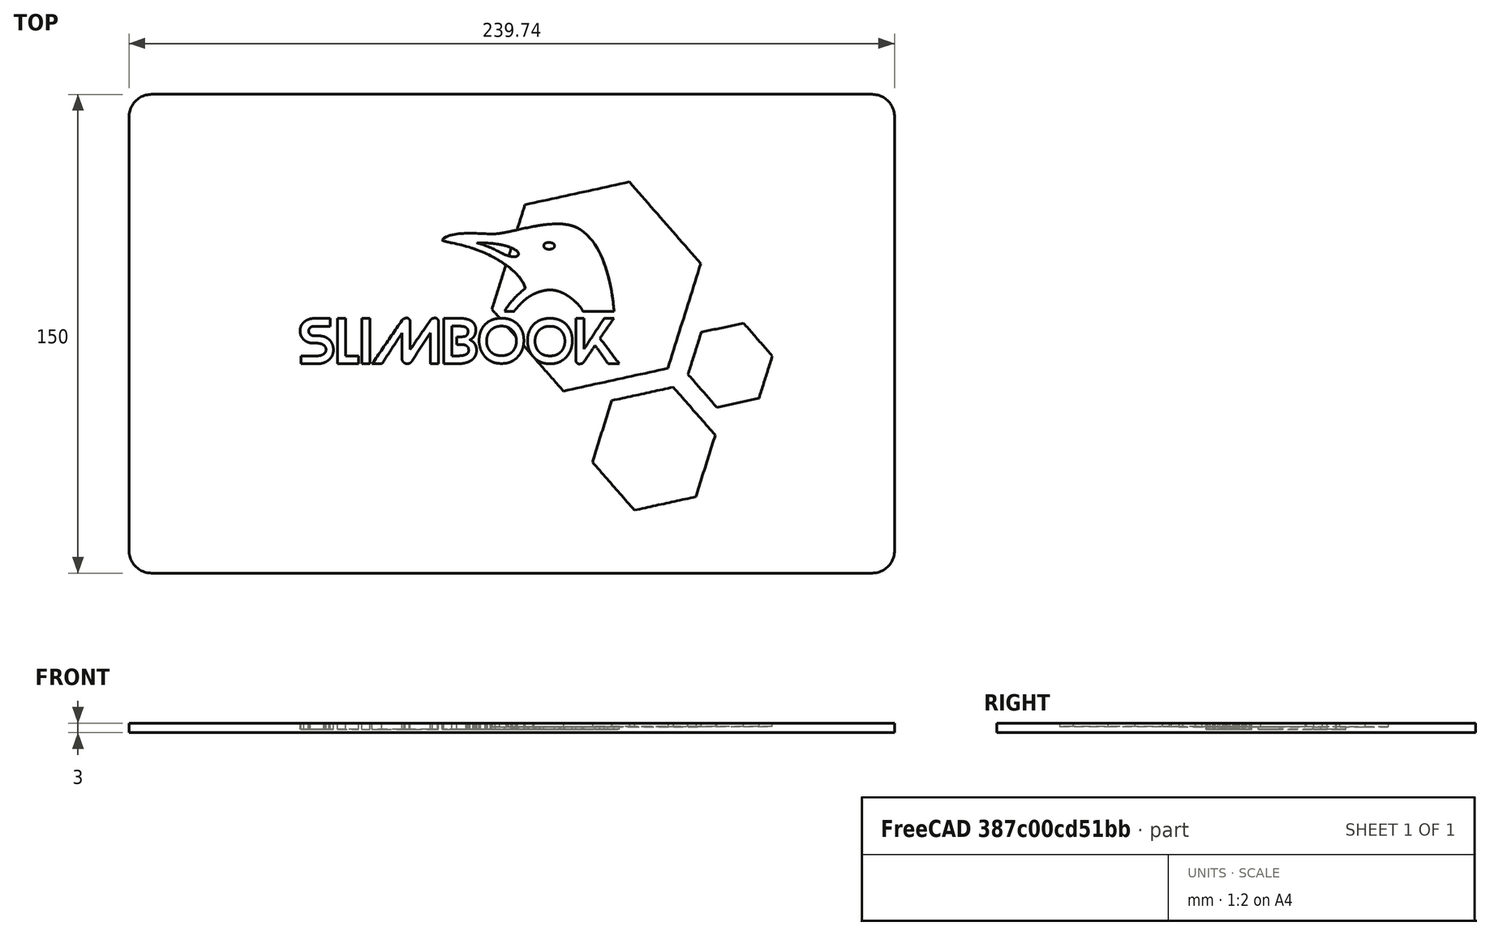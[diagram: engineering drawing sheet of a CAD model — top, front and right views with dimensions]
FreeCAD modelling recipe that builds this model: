
FCSTD DOCUMENT  (FreeCAD 0.20R29603 (Git))
Label: TAPA-CAJA-slimbook
License: All rights reserved
LicenseURL: http://en.wikipedia.org/wiki/All_rights_reserved
objects: Part::Feature×32, Part::Face×29, Part::Cut×12, Part::Extrusion×5, Part::MultiFuse×2, Part::FeaturePython×1
note: 81 computed .brp shape members not serialized (recipe doc carries the construction recipe); baked Part::Feature solids carry a one-line shape summary decoded from their .brp

FEATURE [Part::Feature] rect4531
  shape: bbox 239.7 x 150 x 2e-07 mm, 0 faces, 0 solids (baked)
FEATURE [Part::Feature] path1385_9
  shape: bbox 38.48 x 38.56 x 2.028e-07 mm, 0 faces, 0 solids (baked)
FEATURE [Part::Feature] path1385_9_8
  shape: bbox 26.41 x 26.4 x 2e-07 mm, 0 faces, 0 solids (baked)
FEATURE [Part::Feature] path4723003
  shape: bbox 54.7 x 27.53 x 2.667e-07 mm, 0 faces, 0 solids (baked)
FEATURE [Part::Face] Face001
  FaceMakerClass = Part::FaceMakerBullseye
  Sources = -> [path4723003]
FEATURE [Part::Feature] path4723004
  shape: bbox 3.528 x 2.127 x 2.667e-07 mm, 0 faces, 0 solids (baked)
FEATURE [Part::Feature] path4723005
  shape: bbox 13.37 x 4.768 x 2.667e-07 mm, 0 faces, 0 solids (baked)
FEATURE [Part::Face] Face002
  FaceMakerClass = Part::FaceMakerBullseye
  Sources = -> [path4723004,path4723005]
FEATURE [Part::Cut] Cut035
  Base = -> Face001
  Refine = true
  Tool = -> Face002
FEATURE [Part::Feature] path4723006
  shape: bbox 20.8 x 14.35 x 2.667e-07 mm, 0 faces, 0 solids (baked)
FEATURE [Part::Face] Face003
  FaceMakerClass = Part::FaceMakerBullseye
  Sources = -> [path4723006]
FEATURE [Part::Feature] path4723007
  shape: bbox 13.53 x 14.33 x 2.667e-07 mm, 0 faces, 0 solids (baked)
FEATURE [Part::Face] Face004
  FaceMakerClass = Part::FaceMakerBullseye
  Sources = -> [path4723007]
FEATURE [Part::Feature] path4723008
  shape: bbox 14.02 x 14.18 x 2.667e-07 mm, 0 faces, 0 solids (baked)
FEATURE [Part::Face] Face005
  FaceMakerClass = Part::FaceMakerBullseye
  Sources = -> [path4723008]
FEATURE [Part::Feature] path4723009
  shape: bbox 10.29 x 14.24 x 2.667e-07 mm, 0 faces, 0 solids (baked)
FEATURE [Part::Face] Face010
  FaceMakerClass = Part::FaceMakerBullseye
  Sources = -> [path4723009]
FEATURE [Part::Feature] path4723010
  shape: bbox 10.44 x 14.24 x 2.667e-07 mm, 0 faces, 0 solids (baked)
FEATURE [Part::Face] Face013
  FaceMakerClass = Part::FaceMakerBullseye
  Sources = -> [path4723010]
FEATURE [Part::Feature] path4723011
  shape: bbox 6.55 x 14.24 x 2.667e-07 mm, 0 faces, 0 solids (baked)
FEATURE [Part::Face] Face012
  FaceMakerClass = Part::FaceMakerBullseye
  Sources = -> [path4723011]
FEATURE [Part::Feature] path4723012
  shape: bbox 2.568 x 14.24 x 2.667e-07 mm, 0 faces, 0 solids (baked)
FEATURE [Part::Face] Face011
  FaceMakerClass = Part::FaceMakerBullseye
  Sources = -> [path4723012]
FEATURE [Part::Feature] path4723013
  shape: bbox 14.02 x 14.24 x 2.667e-07 mm, 0 faces, 0 solids (baked)
FEATURE [Part::Face] Face008
  FaceMakerClass = Part::FaceMakerBullseye
  Sources = -> [path4723013]
FEATURE [Part::Feature] path4723014
  shape: bbox 5.247 x 9.291 x 2.667e-07 mm, 0 faces, 0 solids (baked)
FEATURE [Part::Face] Face009
  FaceMakerClass = Part::FaceMakerBullseye
  Sources = -> [path4723014]
FEATURE [Part::Cut] Cut038
  Base = -> Face010
  Refine = true
  Tool = -> Face009
FEATURE [Part::Feature] path4723015
  shape: bbox 9.343 x 9.236 x 2.667e-07 mm, 0 faces, 0 solids (baked)
FEATURE [Part::Face] Face006
  FaceMakerClass = Part::FaceMakerBullseye
  Sources = -> [path4723015]
FEATURE [Part::Cut] Cut036
  Base = -> Face005
  Refine = true
  Tool = -> Face006
FEATURE [Part::Feature] path4723016
  shape: bbox 9.342 x 9.272 x 2.667e-07 mm, 0 faces, 0 solids (baked)
FEATURE [Part::Face] Face007
  FaceMakerClass = Part::FaceMakerBullseye
  Sources = -> [path4723016]
FEATURE [Part::Cut] Cut037
  Base = -> Face008
  Refine = true
  Tool = -> Face007
FEATURE [Part::MultiFuse] Fusion027  label="logo_pinguino"
  Placement = pos=(189,115,0) rot=(0.707107,-0.707107,0;3.14159rad)
  Refine = true
  Shapes = -> [Face013,Cut035,Face003,Face004,Cut036,Cut037,Cut038,Face011,Face012]
FEATURE [Part::Extrusion] Extrude100
  Base = -> Fusion027
  Dir = (1e-16,1e-16,-1)
  DirMode = 2
  FaceMakerClass = Part::FaceMakerBullseye
  LengthFwd = 20
  LengthRev = 0
  Placement = pos=(171,447,-1) rot=(0.707107,-0.707107,0;3.14159rad)
  Solid = false
  Symmetric = false
FEATURE [Part::Feature] path4723017
  shape: bbox 54.7 x 27.53 x 2.667e-07 mm, 0 faces, 0 solids (baked)
FEATURE [Part::Face] Face014
  FaceMakerClass = Part::FaceMakerBullseye
  Sources = -> [path4723017]
FEATURE [Part::Feature] path4723018
  shape: bbox 3.528 x 2.127 x 2.667e-07 mm, 0 faces, 0 solids (baked)
FEATURE [Part::Feature] path4723019
  shape: bbox 13.37 x 4.768 x 2.667e-07 mm, 0 faces, 0 solids (baked)
FEATURE [Part::Face] Face015
  FaceMakerClass = Part::FaceMakerBullseye
  Sources = -> [path4723018,path4723019]
FEATURE [Part::Cut] Cut039
  Base = -> Face014
  Refine = true
  Tool = -> Face015
FEATURE [Part::Feature] path4723020
  shape: bbox 20.8 x 14.35 x 2.667e-07 mm, 0 faces, 0 solids (baked)
FEATURE [Part::Face] Face016
  FaceMakerClass = Part::FaceMakerBullseye
  Sources = -> [path4723020]
FEATURE [Part::Feature] path4723021
  shape: bbox 13.53 x 14.33 x 2.667e-07 mm, 0 faces, 0 solids (baked)
FEATURE [Part::Face] Face017
  FaceMakerClass = Part::FaceMakerBullseye
  Sources = -> [path4723021]
FEATURE [Part::Feature] path4723022
  shape: bbox 14.02 x 14.18 x 2.667e-07 mm, 0 faces, 0 solids (baked)
FEATURE [Part::Face] Face018
  FaceMakerClass = Part::FaceMakerBullseye
  Sources = -> [path4723022]
FEATURE [Part::Feature] path4723023
  shape: bbox 10.29 x 14.24 x 2.667e-07 mm, 0 faces, 0 solids (baked)
FEATURE [Part::Face] Face023
  FaceMakerClass = Part::FaceMakerBullseye
  Sources = -> [path4723023]
FEATURE [Part::Feature] path4723024
  shape: bbox 10.44 x 14.24 x 2.667e-07 mm, 0 faces, 0 solids (baked)
FEATURE [Part::Face] Face026
  FaceMakerClass = Part::FaceMakerBullseye
  Sources = -> [path4723024]
FEATURE [Part::Feature] path4723025
  shape: bbox 6.55 x 14.24 x 2.667e-07 mm, 0 faces, 0 solids (baked)
FEATURE [Part::Face] Face025
  FaceMakerClass = Part::FaceMakerBullseye
  Sources = -> [path4723025]
FEATURE [Part::Feature] path4723026
  shape: bbox 2.568 x 14.24 x 2.667e-07 mm, 0 faces, 0 solids (baked)
FEATURE [Part::Face] Face024
  FaceMakerClass = Part::FaceMakerBullseye
  Sources = -> [path4723026]
FEATURE [Part::Feature] path4723027
  shape: bbox 14.02 x 14.24 x 2.667e-07 mm, 0 faces, 0 solids (baked)
FEATURE [Part::Face] Face021
  FaceMakerClass = Part::FaceMakerBullseye
  Sources = -> [path4723027]
FEATURE [Part::Feature] path4723028
  shape: bbox 5.247 x 9.291 x 2.667e-07 mm, 0 faces, 0 solids (baked)
FEATURE [Part::Face] Face022
  FaceMakerClass = Part::FaceMakerBullseye
  Sources = -> [path4723028]
FEATURE [Part::Cut] Cut042
  Base = -> Face023
  Refine = true
  Tool = -> Face022
FEATURE [Part::Feature] path4723029
  shape: bbox 9.343 x 9.236 x 2.667e-07 mm, 0 faces, 0 solids (baked)
FEATURE [Part::Face] Face019
  FaceMakerClass = Part::FaceMakerBullseye
  Sources = -> [path4723029]
FEATURE [Part::Cut] Cut040
  Base = -> Face018
  Refine = true
  Tool = -> Face019
FEATURE [Part::Feature] path4723030
  shape: bbox 9.342 x 9.272 x 2.667e-07 mm, 0 faces, 0 solids (baked)
FEATURE [Part::Face] Face020
  FaceMakerClass = Part::FaceMakerBullseye
  Sources = -> [path4723030]
FEATURE [Part::Cut] Cut041
  Base = -> Face021
  Refine = true
  Tool = -> Face020
FEATURE [Part::MultiFuse] Fusion028  label="logo_pinguino001"
  Placement = pos=(189,115,0) rot=(0.707107,-0.707107,0;3.14159rad)
  Refine = true
  Shapes = -> [Face026,Cut039,Face016,Face017,Cut040,Cut041,Cut042,Face024,Face025]
FEATURE [Part::Face] Face027
  FaceMakerClass = Part::FaceMakerBullseye
  Sources = -> [path1385_9]
FEATURE [Part::Extrusion] Extrude
  Base = -> path1385_9
  Dir = (0,0,-1)
  DirMode = 2
  FaceMakerClass = Part::FaceMakerBullseye
  LengthFwd = 1
  LengthRev = 0
  Placement = pos=(-17,53,0) rot=(0,0,1;0rad)
  Solid = true
  Symmetric = false
FEATURE [Part::Face] Face028
  FaceMakerClass = Part::FaceMakerBullseye
  Sources = -> [path1385_9_8]
FEATURE [Part::Extrusion] Extrude101
  Base = -> Face028
  Dir = (0,0,1)
  DirMode = 2
  FaceMakerClass = Part::FaceMakerBullseye
  LengthFwd = 1
  LengthRev = 0
  Solid = false
  Symmetric = false
FEATURE [Part::Feature] path1385_010
  shape: bbox 38.48 x 38.56 x 2.028e-07 mm, 0 faces, 0 solids (baked)
FEATURE [Part::Extrusion] Extrude102
  Base = -> path1385_010
  Dir = (0,0,-1)
  DirMode = 2
  FaceMakerClass = Part::FaceMakerBullseye
  LengthFwd = 1
  LengthRev = 0
  Placement = pos=(0,0,1) rot=(0,0,1;0rad)
  Solid = true
  Symmetric = false
FEATURE [Part::FeaturePython] Clone  label="Extrude103"  # Draft clone (typed FeaturePython)
  AttacherType = Attacher::AttachEngine3D
  Fuse = false
  Objects = -> [Extrude]
  Placement = pos=(-134.77,-80.36,1.46) rot=(0,0,1;0rad)
  Scale = (1.7,1.7,1.7)
FEATURE [Part::Face] Face
  FaceMakerClass = Part::FaceMakerBullseye
  Sources = -> [rect4531]
FEATURE [Part::Extrusion] Extrude103  label="Extrude104"
  Base = -> Face
  Dir = (0,0,1)
  DirMode = 2
  FaceMakerClass = Part::FaceMakerBullseye
  LengthFwd = 3
  LengthRev = 0
  Placement = pos=(0,0,-2) rot=(0,0,1;0rad)
  Solid = false
  Symmetric = false
FEATURE [Part::Cut] Cut
  Base = -> Extrude103
  Refine = true
  Tool = -> Clone
FEATURE [Part::Cut] Cut043
  Base = -> Cut
  Refine = true
  Tool = -> Extrude100
FEATURE [Part::Cut] Cut044
  Base = -> Cut043
  Refine = true
  Tool = -> Extrude102
FEATURE [Part::Cut] Cut045
  Base = -> Cut044
  Refine = true
  Tool = -> Extrude101
